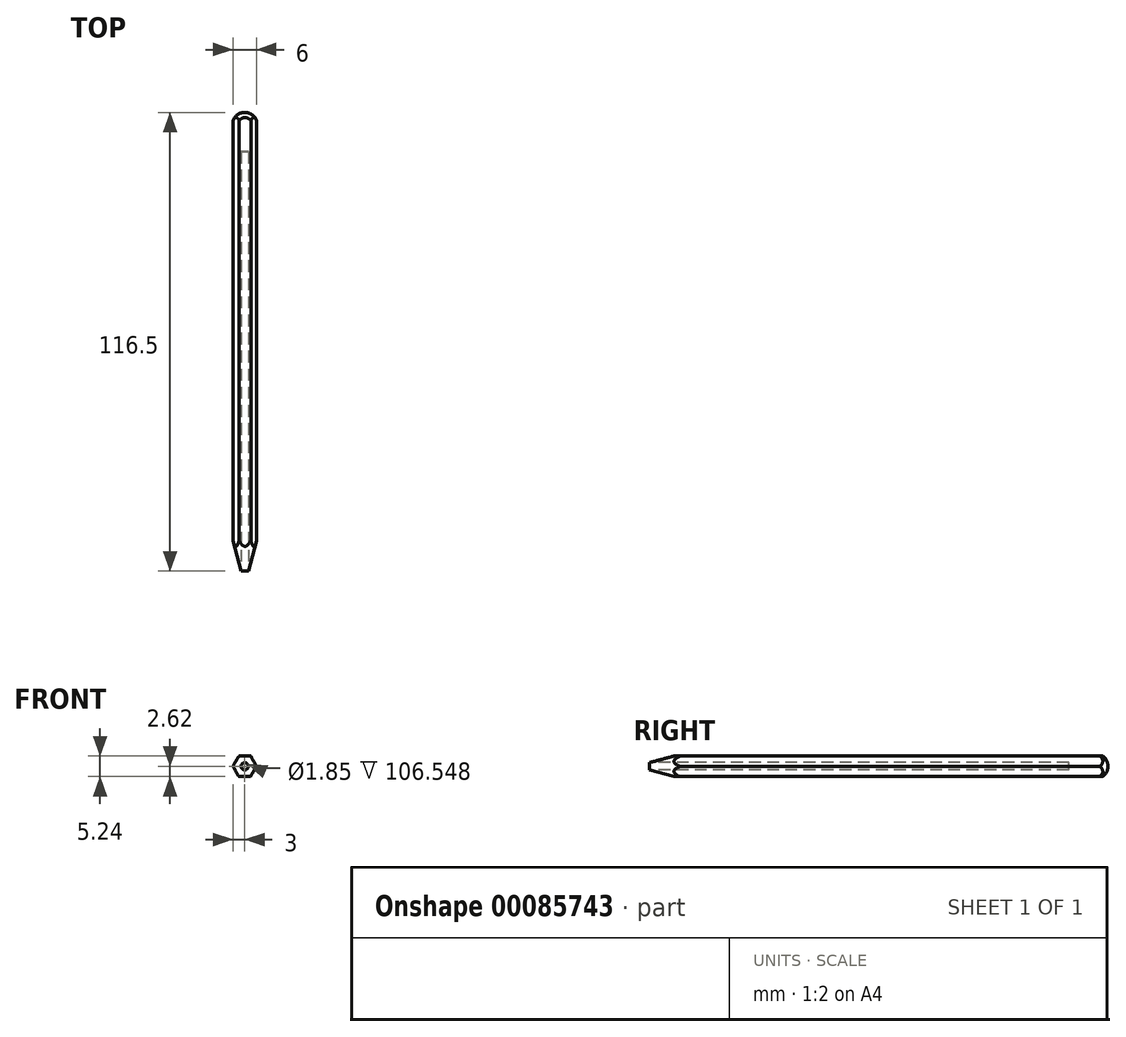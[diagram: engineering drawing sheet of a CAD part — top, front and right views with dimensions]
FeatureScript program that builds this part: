
annotation { "Feature Type Name" : "Feature", "Feature Type Description" : "" }
export const myFeature = defineFeature(function(context is Context, id is Id, definition is map)
    precondition{}
    {
        {
            var Q0;
            Q0=qCreatedBy(makeId("Front.planeOp"),FACE);
            var sketch = newSketch(context, id + "F0", { "sketchPlane" : qUnion([Q0])});
            skCircle(sketch, "E0.cCircle", {"center": v(0, 0) * mm, "radius": 3 * mm, "construction": true});
            skLineSegment(sketch, "E0.0", {"start": v(-1.46, 2.62) * mm, "end": v(1.54, 2.57) * mm});
            skLineSegment(sketch, "E0.1", {"start": v(1.54, 2.57) * mm, "end": v(3, -0.05) * mm});
            skLineSegment(sketch, "E0.2", {"start": v(3, -0.05) * mm, "end": v(1.46, -2.62) * mm});
            skLineSegment(sketch, "E0.3", {"start": v(1.46, -2.62) * mm, "end": v(-1.54, -2.57) * mm});
            skLineSegment(sketch, "E0.4", {"start": v(-1.54, -2.57) * mm, "end": v(-3, 0.05) * mm});
            skLineSegment(sketch, "E0.5", {"start": v(-3, 0.05) * mm, "end": v(-1.46, 2.62) * mm});
            skSolve(sketch);
        }
        {
            var Q0;
            Q0=makeQuery(id+"F0.imprint","IMPRINT",FACE,{"disambiguationData":[TD([[makeQuery(id+"F0.imprint","IMPRINT",EDGE,{"derivedFrom":sQuery(id+"F0.wireOp",EDGE,"E0.0")}),-1.0]])]});
            extrude(context, id + "F1", {"entities" : qUnion([Q0]), "oppositeDirection" : true, "depth" : 120 * mm});
        }
        {
            var Q0;
            Q0=makeQuery(id+"F1.opExtrude","CAP_FACE",FACE,{"disambiguationData":[OSD([sQuery(id+"F0.wireOp",EDGE,"E0.0"),sQuery(id+"F0.wireOp",EDGE,"E0.1"),sQuery(id+"F0.wireOp",EDGE,"E0.2"),sQuery(id+"F0.wireOp",EDGE,"E0.3"),sQuery(id+"F0.wireOp",EDGE,"E0.4"),sQuery(id+"F0.wireOp",EDGE,"E0.5")])],"isStart":true});
            var sketch = newSketch(context, id + "F2", { "sketchPlane" : qUnion([Q0])});
            skCircle(sketch, "E1", {"center": v(0, 0) * mm, "radius": 0.93 * mm});
            skSolve(sketch);
        }
        {
            var Q0;
            Q0=makeQuery(id+"F2.imprint","IMPRINT",FACE,{"disambiguationData":[TD([[makeQuery(id+"F2.imprint","IMPRINT",EDGE,{"derivedFrom":sQuery(id+"F2.wireOp",EDGE,"E1")}),1.0]])]});
            extrude(context, id + "F3", {"entities" : qUnion([Q0]), "operationType" : NewBodyOperationType.REMOVE, "oppositeDirection" : true, "depth" : 110 * mm});
        }
        {
            var Q0;
            Q0=qCreatedBy(makeId("Right.planeOp"),FACE);
            var sketch = newSketch(context, id + "F4", { "sketchPlane" : qUnion([Q0])});
            skLineSegment(sketch, "E2", {"start": v(-44.03, 0) * mm, "end": v(99.65, 0) * mm});
            skArc(sketch, "E3", {"start": v(12.07, 3.24) * mm, "mid": v(-12.5, 0) * mm, "end": v(12.07, -3.24) * mm});
            skLineSegment(sketch, "E4", {"start": v(12.07, 3.24) * mm, "end": v(0, 0) * mm});
            skLineSegment(sketch, "E5", {"start": v(12.07, -3.24) * mm, "end": v(0, 0) * mm});
            skSolve(sketch);
        }
        {
            var Q0;
            {var subQ0=sQuery(id+"F4.wireOp",EDGE,"E4");Q0=makeQuery(id+"F4.imprint","IMPRINT",FACE,{"disambiguationData":[TD([[makeQuery(id+"F4.imprint","IMPRINT",EDGE,{"derivedFrom":subQ0}),-1.0]])]});}
            var Q1;
            Q1=sQuery(id+"F4.wireOp",EDGE,"E2");
            revolve(context, id + "F5", {"operationType" : NewBodyOperationType.REMOVE, "entities" : qUnion([Q0]), "axis" : qUnion([Q1]), "revolveType" : RevolveType.FULL, "oppositeDirection" : true});
        }
        {
            var Q0;
            Q0=makeQuery(id+"F1.opExtrude","SWEPT_BODY",BODY,{"disambiguationData":[OSD([sQuery(id+"F0.wireOp",EDGE,"E0.0"),sQuery(id+"F0.wireOp",EDGE,"E0.1"),sQuery(id+"F0.wireOp",EDGE,"E0.2"),sQuery(id+"F0.wireOp",EDGE,"E0.3"),sQuery(id+"F0.wireOp",EDGE,"E0.4"),sQuery(id+"F0.wireOp",EDGE,"E0.5")])]});
            transform(context, id + "F6", {"entities" : qUnion([Q0]), "transformType" : TransformType.TRANSLATION_3D, "dx" : 0 * mm, "dy" : 0 * mm, "dz" : 81.08 * mm, "makeCopy" : true});
        }
        {
            var Q0;
            Q0=makeQuery(id+"F6.opPattern","COPY",BODY,{"derivedFrom":makeQuery(id+"F1.opExtrude","SWEPT_BODY",BODY,{"disambiguationData":[OSD([sQuery(id+"F0.wireOp",EDGE,"E0.0"),sQuery(id+"F0.wireOp",EDGE,"E0.1"),sQuery(id+"F0.wireOp",EDGE,"E0.2"),sQuery(id+"F0.wireOp",EDGE,"E0.3"),sQuery(id+"F0.wireOp",EDGE,"E0.4"),sQuery(id+"F0.wireOp",EDGE,"E0.5")])]}),"instanceName":"1"});
            deleteBodies(context, id + "F7", {"entities" : qUnion([Q0])});
        }
        {
            var Q0;
            Q0=qCreatedBy(makeId("Right.planeOp"),FACE);
            var sketch = newSketch(context, id + "F8", { "sketchPlane" : qUnion([Q0])});
            skArc(sketch, "E6", {"start": v(116.75, -3.2) * mm, "mid": v(119.95, 0) * mm, "end": v(116.75, 3.2) * mm});
            skLineSegment(sketch, "E7", {"start": v(0, 0) * mm, "end": v(170.86, 0) * mm});
            skLineSegment(sketch, "E8", {"start": v(116.75, 0) * mm, "end": v(116.75, 8.28) * mm});
            skLineSegment(sketch, "E9", {"start": v(116.75, 0) * mm, "end": v(116.75, -4.73) * mm});
            skLineSegment(sketch, "E10", {"start": v(116.75, 3.2) * mm, "end": v(138.86, 3.2) * mm});
            skLineSegment(sketch, "E11", {"start": v(116.75, -3.2) * mm, "end": v(139.32, -3.2) * mm});
            skLineSegment(sketch, "E12", {"start": v(139.32, -3.2) * mm, "end": v(138.86, 3.2) * mm});
            skSolve(sketch);
        }
        {
            var Q0;
            {var subQ0=sQuery(id+"F8.wireOp",EDGE,"E10");Q0=makeQuery(id+"F8.imprint","IMPRINT",FACE,{"disambiguationData":[TD([[makeQuery(id+"F8.imprint","IMPRINT",EDGE,{"derivedFrom":subQ0}),-1.0]])]});}
            var Q1;
            Q1=sQuery(id+"F8.wireOp",EDGE,"E7");
            revolve(context, id + "F9", {"operationType" : NewBodyOperationType.REMOVE, "entities" : qUnion([Q0]), "axis" : qUnion([Q1]), "revolveType" : RevolveType.FULL});
        }
    });
